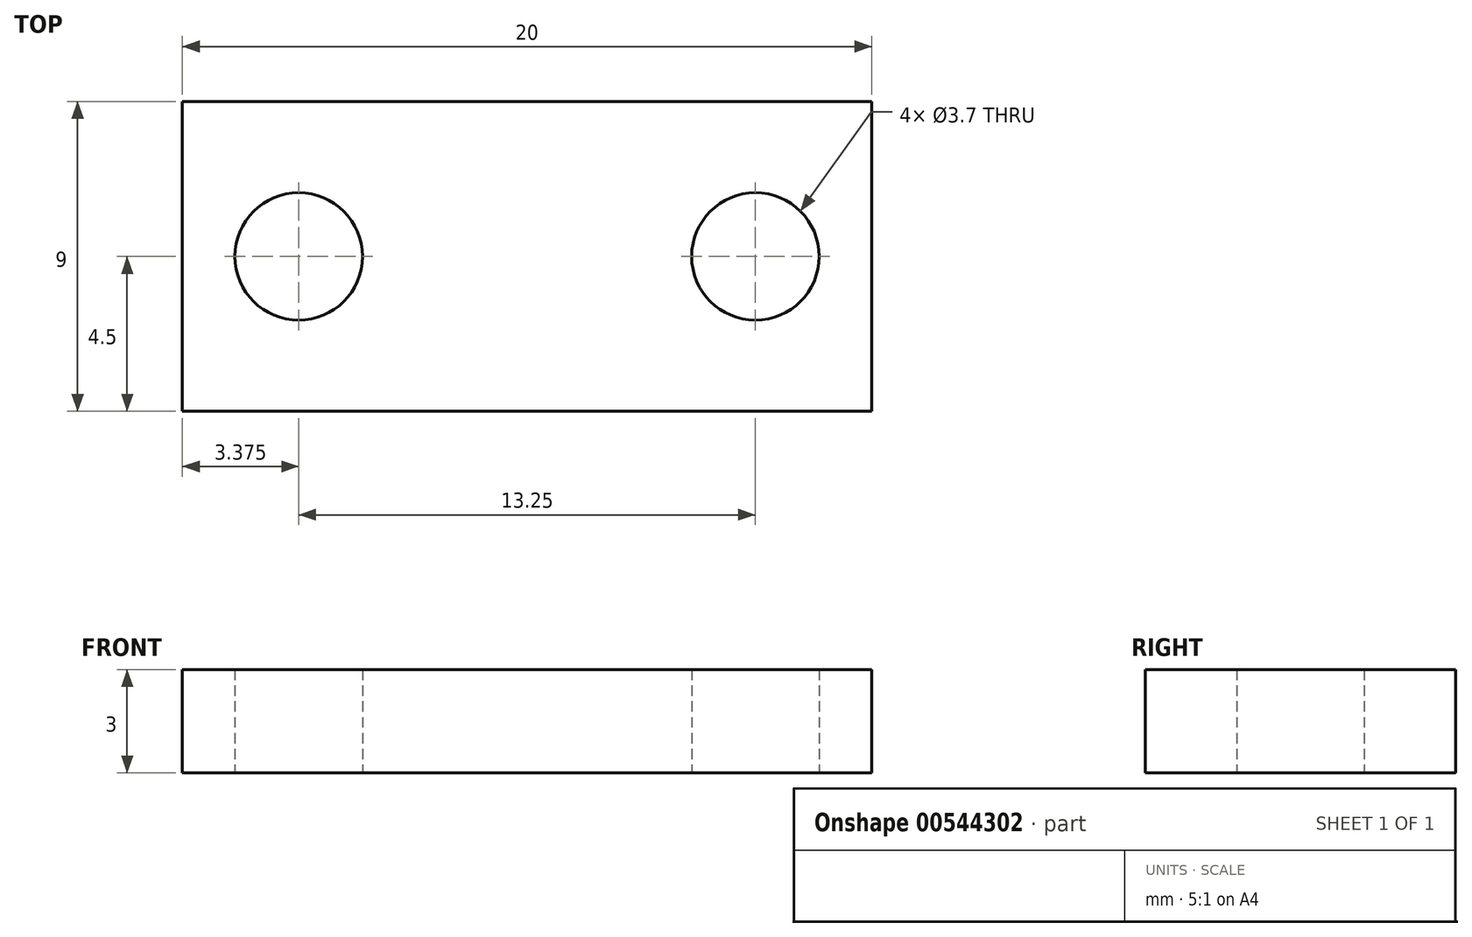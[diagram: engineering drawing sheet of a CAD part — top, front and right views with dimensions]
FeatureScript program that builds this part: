
annotation { "Feature Type Name" : "Feature", "Feature Type Description" : "" }
export const myFeature = defineFeature(function(context is Context, id is Id, definition is map)
    precondition{}
    {
        {
            var Q0;
            Q0=qCreatedBy(makeId("Top.planeOp"),FACE);
            var sketch = newSketch(context, id + "F0", { "sketchPlane" : qUnion([Q0])});
            skLineSegment(sketch, "E0.bottom", {"start": v(10, 4.5) * mm, "end": v(-10, 4.5) * mm});
            skLineSegment(sketch, "E0.top", {"start": v(10, -4.5) * mm, "end": v(-10, -4.5) * mm});
            skLineSegment(sketch, "E0.left", {"start": v(10, 4.5) * mm, "end": v(10, -4.5) * mm});
            skLineSegment(sketch, "E0.right", {"start": v(-10, 4.5) * mm, "end": v(-10, -4.5) * mm});
            skPoint(sketch, "E0.middle", {"position": v(0, 0) * mm});
            skLineSegment(sketch, "E1", {"start": v(0, 0) * mm, "end": v(0, 4.5) * mm, "construction": true});
            skCircle(sketch, "E2", {"center": v(-6.62, 0) * mm, "radius": 1.85 * mm});
            skCircle(sketch, "E3.MirrorC", {"center": v(6.62, 0) * mm, "radius": 1.85 * mm});
            skSolve(sketch);
        }
        {
            var Q0;
            Q0=makeQuery(id+"F0.imprint","IMPRINT",FACE,{"disambiguationData":[TD([[makeQuery(id+"F0.imprint","IMPRINT",EDGE,{"derivedFrom":sQuery(id+"F0.wireOp",EDGE,"E0.bottom")}),1.0]])]});
            extrude(context, id + "F1", {"entities" : qUnion([Q0]), "depth" : 3 * mm, "offsetDistance" : 25 * mm});
        }
    });
